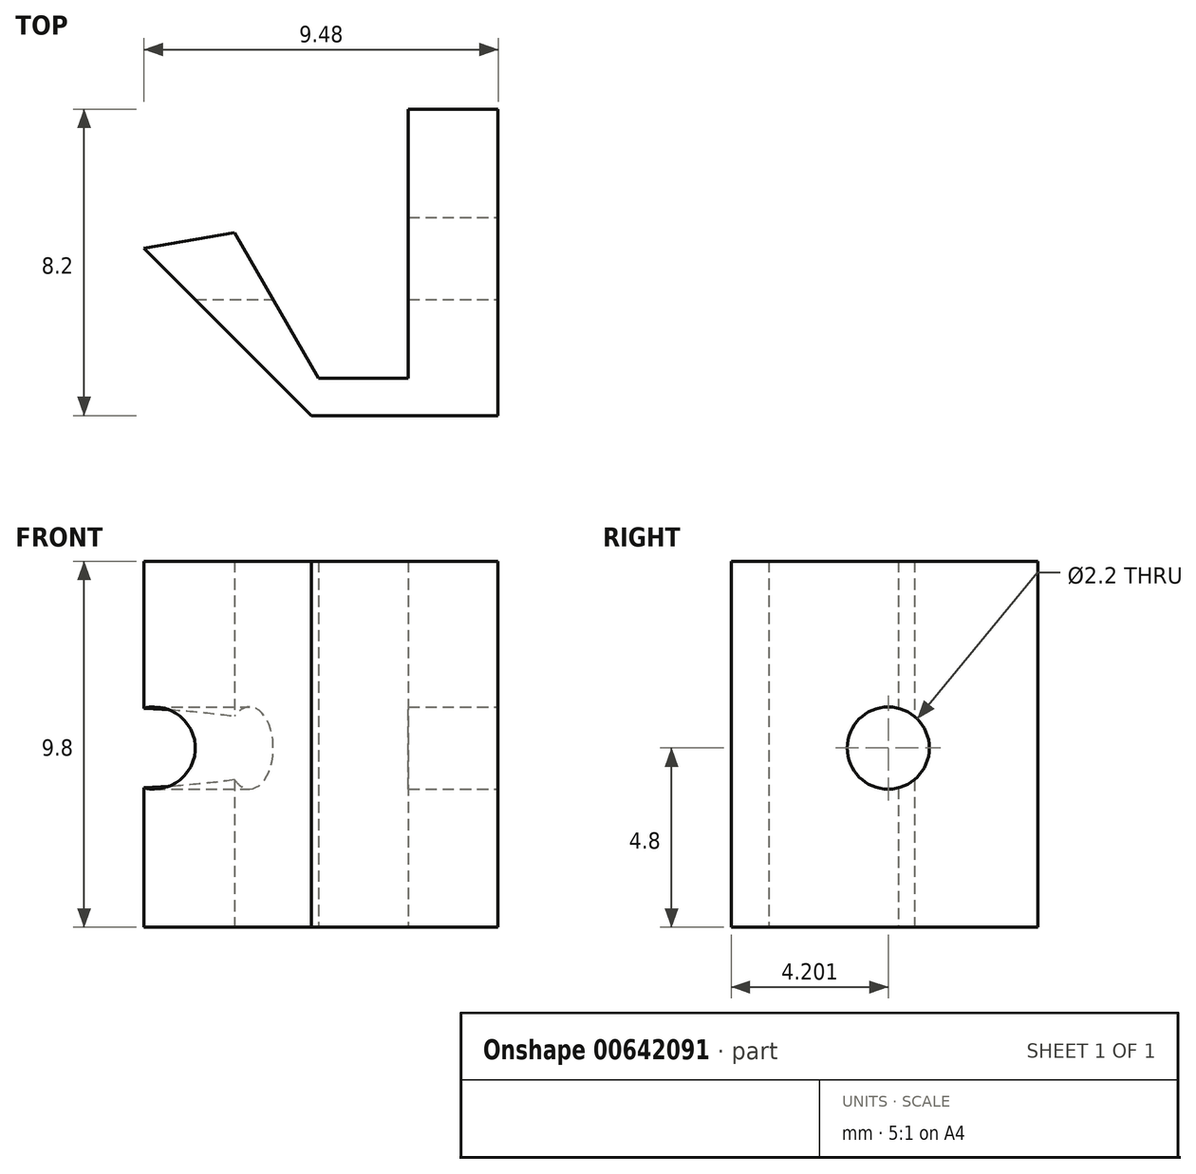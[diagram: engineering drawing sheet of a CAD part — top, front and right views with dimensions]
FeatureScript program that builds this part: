
annotation { "Feature Type Name" : "Feature", "Feature Type Description" : "" }
export const myFeature = defineFeature(function(context is Context, id is Id, definition is map)
    precondition{}
    {
        {
            var Q0;
            Q0=qCreatedBy(makeId("Top.planeOp"),FACE);
            var sketch = newSketch(context, id + "F0", { "sketchPlane" : qUnion([Q0])});
            skLineSegment(sketch, "E0", {"start": v(-30.3, -0.15) * mm, "end": v(-25.3, -0.15) * mm});
            skLineSegment(sketch, "E1", {"start": v(-25.3, -0.15) * mm, "end": v(-25.3, 8.05) * mm});
            skLineSegment(sketch, "E2", {"start": v(-25.3, 8.05) * mm, "end": v(-27.7, 8.05) * mm});
            skLineSegment(sketch, "E3", {"start": v(-27.7, 8.05) * mm, "end": v(-27.7, 0.85) * mm});
            skLineSegment(sketch, "E4", {"start": v(-27.7, 0.85) * mm, "end": v(-30.1, 0.85) * mm});
            skLineSegment(sketch, "E5", {"start": v(-30.1, 0.85) * mm, "end": v(-32.35, 4.75) * mm});
            skLineSegment(sketch, "E6", {"start": v(-34.78, 4.32) * mm, "end": v(-30.3, -0.15) * mm});
            skLineSegment(sketch, "E7", {"start": v(-34.78, 4.32) * mm, "end": v(-32.35, 4.75) * mm});
            skSolve(sketch);
        }
        {
            var Q0;
            Q0=makeQuery(id+"F0.imprint","IMPRINT",FACE,{"disambiguationData":[TD([[makeQuery(id+"F0.imprint","IMPRINT",EDGE,{"derivedFrom":sQuery(id+"F0.wireOp",EDGE,"E0")}),1.0]])]});
            extrude(context, id + "F1", {"entities" : qUnion([Q0]), "depth" : 9.8 * mm, "offsetDistance" : 25 * mm});
        }
        {
            var Q0;
            Q0=qCreatedBy(makeId("Right.planeOp"),FACE);
            var sketch = newSketch(context, id + "F2", { "sketchPlane" : qUnion([Q0])});
            skLineSegment(sketch, "E8.0", {"start": v(-0.15, 9.8) * mm, "end": v(-0.15, 0) * mm});
            skLineSegment(sketch, "E9.0", {"start": v(-0.15, 0) * mm, "end": v(8.05, 0) * mm});
            skLineSegment(sketch, "E9.1", {"start": v(8.05, 9.8) * mm, "end": v(8.05, 0) * mm});
            skLineSegment(sketch, "E9.2", {"start": v(-0.15, 9.8) * mm, "end": v(8.05, 9.8) * mm});
            skPoint(sketch, "E10", {"position": v(4.05, 4.8) * mm});
            skSolve(sketch);
        }
        {
            var Q0;
            Q0=sQuery(id+"F2.wireOp",VERTEX,"E10");
            var Q1;
            Q1=makeQuery(id+"F1.opExtrude","SWEPT_BODY",BODY,{"disambiguationData":[OSD([sQuery(id+"F0.wireOp",EDGE,"E0"),sQuery(id+"F0.wireOp",EDGE,"E1"),sQuery(id+"F0.wireOp",EDGE,"E2"),sQuery(id+"F0.wireOp",EDGE,"E3"),sQuery(id+"F0.wireOp",EDGE,"E4"),sQuery(id+"F0.wireOp",EDGE,"E5"),sQuery(id+"F0.wireOp",EDGE,"6VcuIoPc-BrWo-LBYm-p6kH-N6J6VejW8XUz"),sQuery(id+"F0.wireOp",EDGE,"Kcg7mSg2-TkDd-RqRM-ZHyW-69ltms5b5Kka"),sQuery(id+"F0.wireOp",EDGE,"0e6765e6-2bf8-4f0d-9507-27d04c5a22c0.filletArc")])]});
            hole(context, id + "F3", {"style" : HoleStyle.SIMPLE, "endStyle" : HoleEndStyle.THROUGH, "holeDiameter" : 2.2 * mm, "majorDiameter" : 5 * mm, "isTappedThrough" : true, "tappedDepth" : 12 * mm, "tapClearance" : 3, "startFromSketch" : true, "locations" : qUnion([Q0]), "scope" : qUnion([Q1])});
        }
    });
